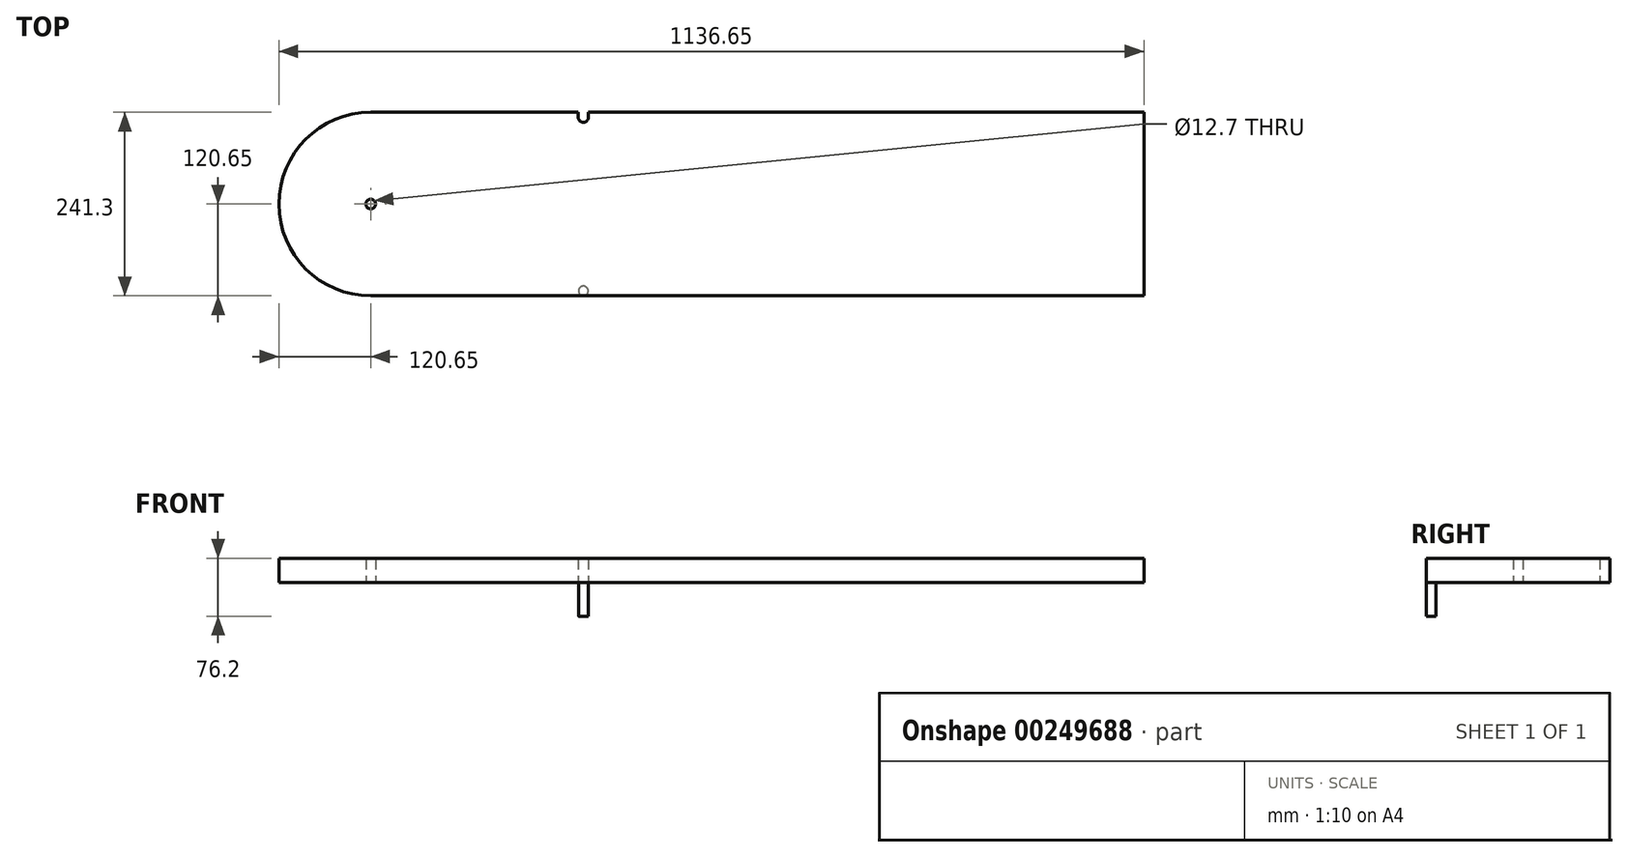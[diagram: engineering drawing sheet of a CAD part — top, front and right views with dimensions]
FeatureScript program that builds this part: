
annotation { "Feature Type Name" : "Feature", "Feature Type Description" : "" }
export const myFeature = defineFeature(function(context is Context, id is Id, definition is map)
    precondition{}
    {
        {
            var Q0;
            Q0=qCreatedBy(makeId("Top.planeOp"),FACE);
            var sketch = newSketch(context, id + "F0", { "sketchPlane" : qUnion([Q0])});
            skArc(sketch, "E0", {"start": v(0, 120.65) * mm, "mid": v(-120.65, 0) * mm, "end": v(0, -120.65) * mm});
            skLineSegment(sketch, "E1", {"start": v(0, 120.65) * mm, "end": v(1016, 120.65) * mm});
            skLineSegment(sketch, "E2", {"start": v(0, -120.65) * mm, "end": v(1016, -120.65) * mm});
            skLineSegment(sketch, "E3", {"start": v(1016, -120.65) * mm, "end": v(1016, 120.65) * mm});
            skCircle(sketch, "E4", {"center": v(0, 0) * mm, "radius": 6.35 * mm});
            skSolve(sketch);
        }
        {
            var Q0;
            Q0 = qSketchRegion(id + "F0", true);
            extrude(context, id + "F1", {"entities" : qUnion([Q0]), "depth" : 31.75 * mm});
        }
        {
            var Q0;
            Q0=makeQuery(id+"F1.opExtrude","CAP_FACE",FACE,{"disambiguationData":[OSD([sQuery(id+"F0.wireOp",EDGE,"E0"),sQuery(id+"F0.wireOp",EDGE,"E1"),sQuery(id+"F0.wireOp",EDGE,"E2"),sQuery(id+"F0.wireOp",EDGE,"E3"),sQuery(id+"F0.wireOp",EDGE,"E4")])],"isStart":true});
            var sketch = newSketch(context, id + "F2", { "sketchPlane" : qUnion([Q0])});
            skCircle(sketch, "E5", {"center": v(279.4, 114.3) * mm, "radius": 6.35 * mm});
            skSolve(sketch);
        }
        {
            var Q0;
            Q0 = qSketchRegion(id + "F2", true);
            extrude(context, id + "F3", {"entities" : qUnion([Q0]), "operationType" : NewBodyOperationType.ADD, "depth" : 44.45 * mm});
        }
        {
            var Q0;
            Q0=makeQuery(id+"F1.opExtrude","CAP_FACE",FACE,{"disambiguationData":[OSD([sQuery(id+"F0.wireOp",EDGE,"E0"),sQuery(id+"F0.wireOp",EDGE,"E1"),sQuery(id+"F0.wireOp",EDGE,"E2"),sQuery(id+"F0.wireOp",EDGE,"E3"),sQuery(id+"F0.wireOp",EDGE,"E4")])],"isStart":true});
            var sketch = newSketch(context, id + "F4", { "sketchPlane" : qUnion([Q0])});
            skArc(sketch, "E6", {"start": v(286, -114.05) * mm, "mid": v(279.4, -107.44) * mm, "end": v(272.8, -114.05) * mm});
            skLineSegment(sketch, "E7", {"start": v(272.8, -114.05) * mm, "end": v(272.8, -120.65) * mm});
            skLineSegment(sketch, "E8", {"start": v(272.8, -120.65) * mm, "end": v(286, -120.65) * mm});
            skLineSegment(sketch, "E9", {"start": v(286, -120.65) * mm, "end": v(286, -114.05) * mm});
            skSolve(sketch);
        }
        {
            var Q0;
            Q0 = qSketchRegion(id + "F4", true);
            extrude(context, id + "F5", {"entities" : qUnion([Q0]), "operationType" : NewBodyOperationType.REMOVE, "oppositeDirection" : true, "depth" : 31.75 * mm});
        }
    });
